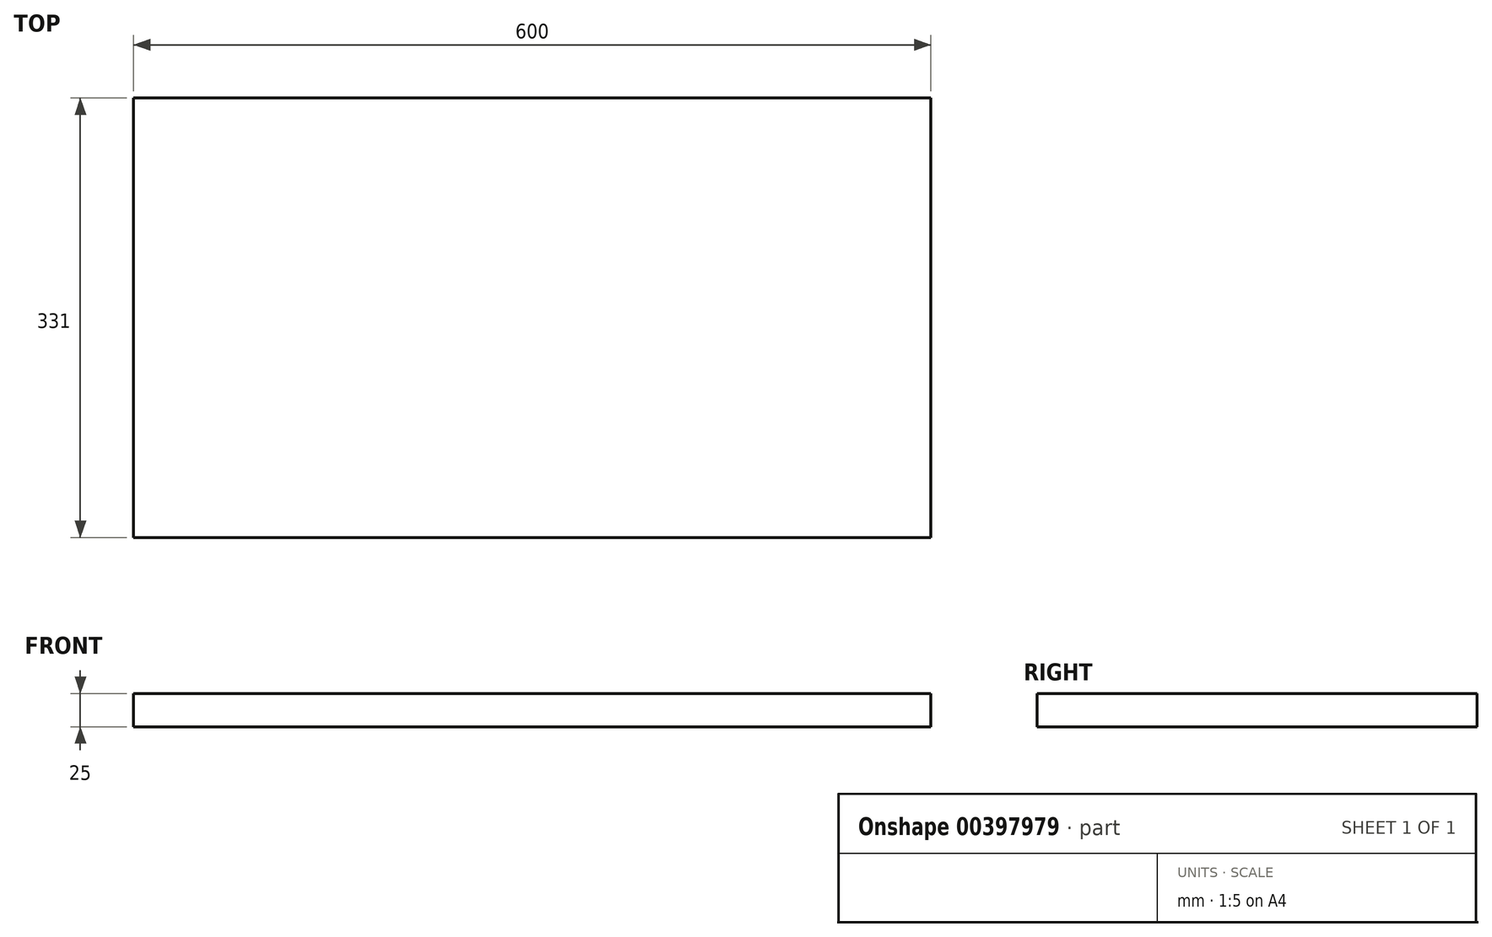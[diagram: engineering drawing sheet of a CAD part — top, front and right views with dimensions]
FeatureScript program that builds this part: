
annotation { "Feature Type Name" : "Feature", "Feature Type Description" : "" }
export const myFeature = defineFeature(function(context is Context, id is Id, definition is map)
    precondition{}
    {
        {
            var Q0;
            Q0=qCreatedBy(makeId("Front.planeOp"),FACE);
            var sketch = newSketch(context, id + "F0", { "sketchPlane" : qUnion([Q0])});
            skLineSegment(sketch, "E0.bottom", {"start": v(-300, 12.5) * mm, "end": v(300, 12.5) * mm});
            skLineSegment(sketch, "E0.top", {"start": v(-300, -12.5) * mm, "end": v(300, -12.5) * mm});
            skLineSegment(sketch, "E0.left", {"start": v(-300, 12.5) * mm, "end": v(-300, -12.5) * mm});
            skLineSegment(sketch, "E0.right", {"start": v(300, 12.5) * mm, "end": v(300, -12.5) * mm});
            skLineSegment(sketch, "E1", {"start": v(0, 12.5) * mm, "end": v(0, -12.5) * mm});
            skSolve(sketch);
        }
        {
            var Q0;
            Q0 = qSketchRegion(id + "F0", true);
            extrude(context, id + "F1", {"entities" : qUnion([Q0]), "depth" : 331 * mm});
        }
    });
